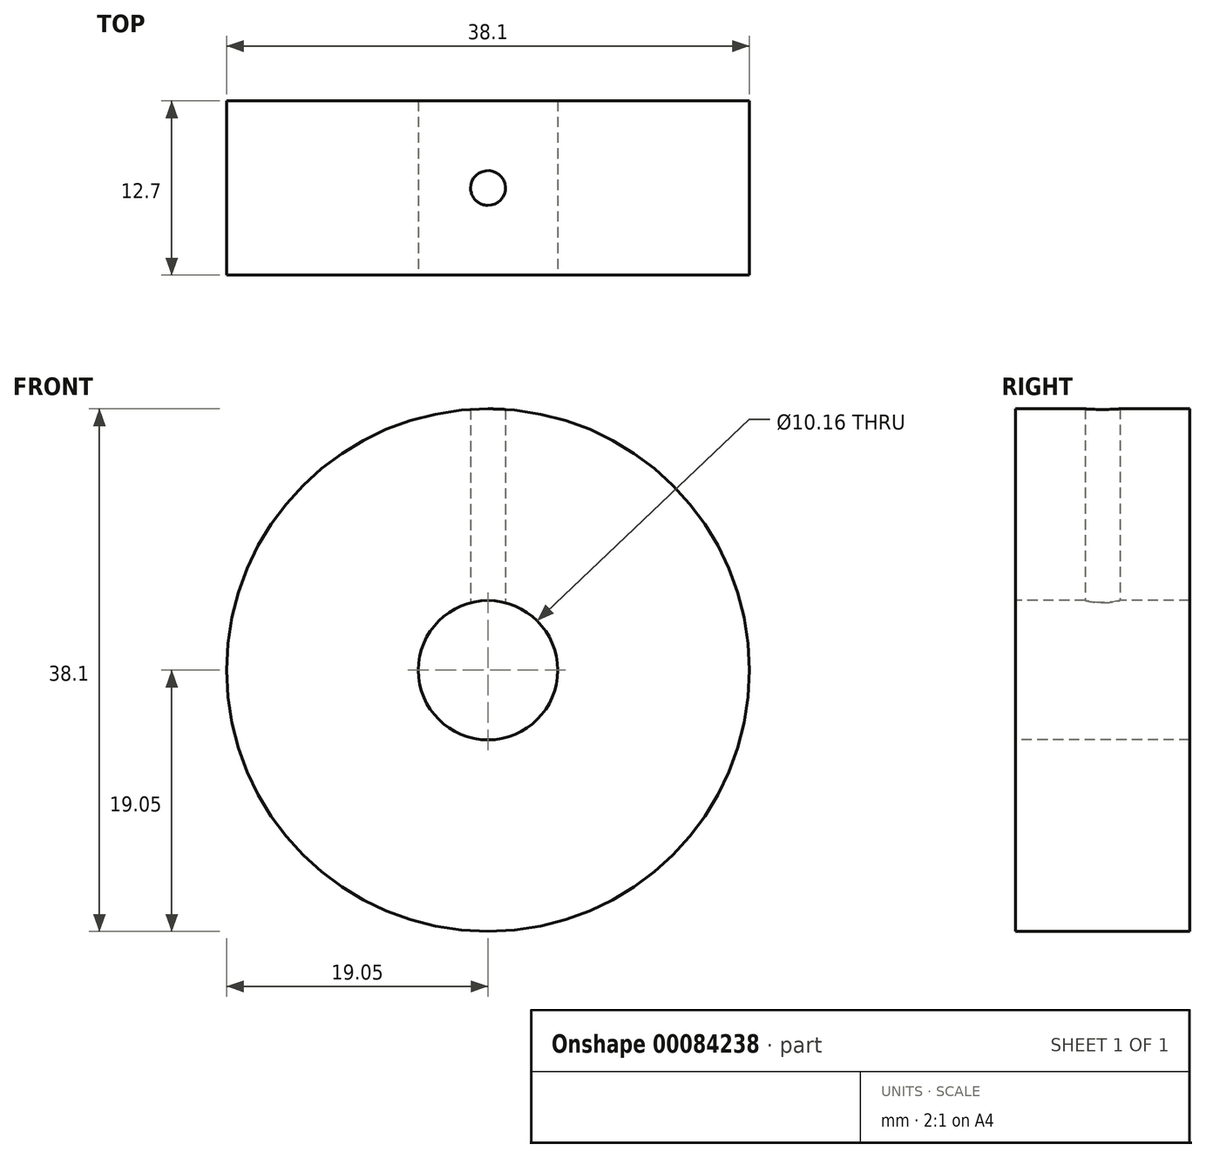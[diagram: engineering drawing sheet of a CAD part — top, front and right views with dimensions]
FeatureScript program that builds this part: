
annotation { "Feature Type Name" : "Feature", "Feature Type Description" : "" }
export const myFeature = defineFeature(function(context is Context, id is Id, definition is map)
    precondition{}
    {
        {
            var Q0;
            Q0=qCreatedBy(makeId("Front.planeOp"),FACE);
            var sketch = newSketch(context, id + "F0", { "sketchPlane" : qUnion([Q0])});
            skCircle(sketch, "E0", {"center": v(0, 0) * mm, "radius": 100.24 * mm});
            skLineSegment(sketch, "E1", {"start": v(-63.5, 77.56) * mm, "end": v(63.5, 77.56) * mm});
            skPoint(sketch, "E2", {"position": v(0, 77.56) * mm});
            skLineSegment(sketch, "E3", {"start": v(0, 77.56) * mm, "end": v(0, 100.24) * mm});
            skLineSegment(sketch, "E4", {"start": v(0, 77.56) * mm, "end": v(0, -100.24) * mm, "construction": true});
            skLineSegment(sketch, "E5", {"start": v(0, 0) * mm, "end": v(100.24, 0) * mm, "construction": true});
            skSolve(sketch);
        }
        {
            var Q0;
            Q0=qCreatedBy(makeId("Front.planeOp"),FACE);
            var sketch = newSketch(context, id + "F1", { "sketchPlane" : qUnion([Q0])});
            skCircle(sketch, "E6.0", {"center": v(0, 0) * mm, "radius": 100.24 * mm, "construction": true});
            skLineSegment(sketch, "E7", {"start": v(0, 0) * mm, "end": v(0, 100.24) * mm});
            skArc(sketch, "E8", {"start": v(0, 93.89) * mm, "mid": v(6.35, 100.24) * mm, "end": v(0, 106.59) * mm});
            skLineSegment(sketch, "E9", {"start": v(0, 93.89) * mm, "end": v(0, 106.59) * mm, "construction": true});
            skSolve(sketch);
        }
        {
            var Q0;
            Q0=sQuery(id+"F1.wireOp",EDGE,"E8");
            var Q1;
            Q1=sQuery(id+"F1.wireOp",EDGE,"E9");
            revolve(context, id + "F2", {"bodyType" : ToolBodyType.SURFACE, "surfaceEntities" : qUnion([Q0]), "axis" : qUnion([Q1]), "revolveType" : RevolveType.FULL});
        }
        {
            var Q0;
            {var subQ0=sQuery(id+"F0.wireOp",EDGE,"E1");var subQ1=sQuery(id+"F0.wireOp",EDGE,"E0");var subQ2=makeQuery(id+"F0.imprint","INTERSECT",VERTEX,{"disambiguationData":[OD(0.0)],"derivedFrom":[subQ1,subQ0]});Q0=makeQuery(id+"F0.imprint","IMPRINT",FACE,{"disambiguationData":[TD([[makeQuery(id+"F0.imprint","IMPRINT",EDGE,{"disambiguationData":[TD([[subQ2,-1.0]])],"derivedFrom":subQ1}),1.0]])]});}
            var sketch = newSketch(context, id + "F3", { "sketchPlane" : qUnion([Q0])});
            skCircle(sketch, "E10", {"center": v(0, 0) * mm, "radius": 19.05 * mm});
            skSolve(sketch);
        }
        {
            var Q0;
            Q0 = qSketchRegion(id + "F3", true);
            extrude(context, id + "F4", {"entities" : qUnion([Q0]), "endBound" : BoundingType.SYMMETRIC, "depth" : 12.7 * mm});
        }
        {
            var Q0;
            Q0=qCreatedBy(makeId("Top.planeOp"),FACE);
            var sketch = newSketch(context, id + "F5", { "sketchPlane" : qUnion([Q0])});
            skCircle(sketch, "E11", {"center": v(0, 0) * mm, "radius": 1.27 * mm});
            skSolve(sketch);
        }
        {
            var Q0;
            Q0 = qSketchRegion(id + "F5", true);
            extrude(context, id + "F6", {"entities" : qUnion([Q0]), "depth" : 102.7 * mm});
        }
        {
            var Q0;
            Q0=makeQuery(id+"F4.opExtrude","CAP_FACE",FACE,{"disambiguationData":[OSD([sQuery(id+"F3.wireOp",EDGE,"E10")])],"isStart":false});
            var sketch = newSketch(context, id + "F7", { "sketchPlane" : qUnion([Q0])});
            skCircle(sketch, "E12", {"center": v(0, 0) * mm, "radius": 5.08 * mm});
            skSolve(sketch);
        }
        {
            var Q0;
            Q0=makeQuery(id+"F7.imprint","IMPRINT",FACE,{"disambiguationData":[TD([[makeQuery(id+"F7.imprint","IMPRINT",EDGE,{"derivedFrom":sQuery(id+"F7.wireOp",EDGE,"E12")}),1.0]])]});
            var Q1;
            Q1=sQuery(id+"F7.wireOp",EDGE,"E12");
            extrude(context, id + "F8", {"entities" : qUnion([Q0]), "operationType" : NewBodyOperationType.REMOVE, "surfaceEntities" : qUnion([Q1]), "endBound" : BoundingType.THROUGH_ALL, "oppositeDirection" : true, "depth" : 25.4 * mm});
        }
        {
            var Q0;
            Q0 = qSketchRegion(id + "F5", true);
            extrude(context, id + "F9", {"entities" : qUnion([Q0]), "operationType" : NewBodyOperationType.REMOVE, "depth" : 109.04 * mm});
        }
    });
